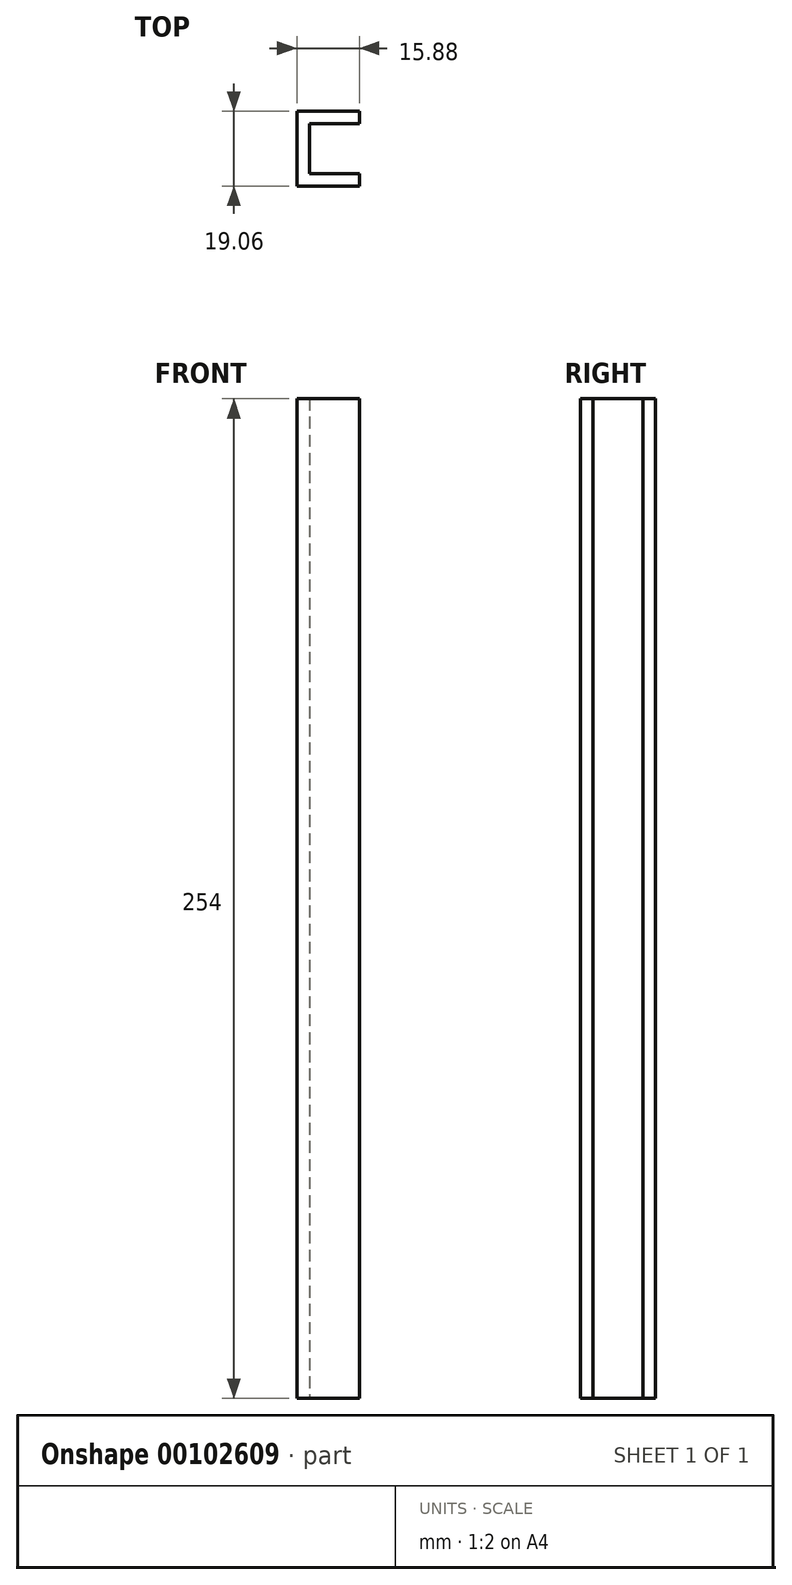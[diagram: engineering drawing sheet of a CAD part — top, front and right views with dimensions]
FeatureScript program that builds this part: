
annotation { "Feature Type Name" : "Feature", "Feature Type Description" : "" }
export const myFeature = defineFeature(function(context is Context, id is Id, definition is map)
    precondition{}
    {
        {
            var Q0;
            Q0=qCreatedBy(makeId("Top.planeOp"),FACE);
            var sketch = newSketch(context, id + "F0", { "sketchPlane" : qUnion([Q0])});
            skLineSegment(sketch, "E0", {"start": v(6.35, 9.53) * mm, "end": v(6.35, 6.35) * mm});
            skLineSegment(sketch, "E1", {"start": v(6.35, 6.35) * mm, "end": v(-6.35, 6.35) * mm});
            skLineSegment(sketch, "E2", {"start": v(-6.35, 6.35) * mm, "end": v(-6.35, -6.35) * mm});
            skLineSegment(sketch, "E3", {"start": v(-6.35, -6.35) * mm, "end": v(6.35, -6.35) * mm});
            skLineSegment(sketch, "E4", {"start": v(6.35, -6.35) * mm, "end": v(6.35, -9.52) * mm});
            skLineSegment(sketch, "E5", {"start": v(6.35, -9.52) * mm, "end": v(-9.52, -9.53) * mm});
            skLineSegment(sketch, "E6", {"start": v(-9.52, -9.53) * mm, "end": v(-9.53, 9.52) * mm});
            skLineSegment(sketch, "E7", {"start": v(-9.53, 9.52) * mm, "end": v(6.35, 9.53) * mm});
            skSolve(sketch);
        }
        {
            var Q0;
            Q0 = qSketchRegion(id + "F0", true);
            extrude(context, id + "F1", {"entities" : qUnion([Q0]), "endBound" : BoundingType.SYMMETRIC, "depth" : 254 * mm});
        }
    });
